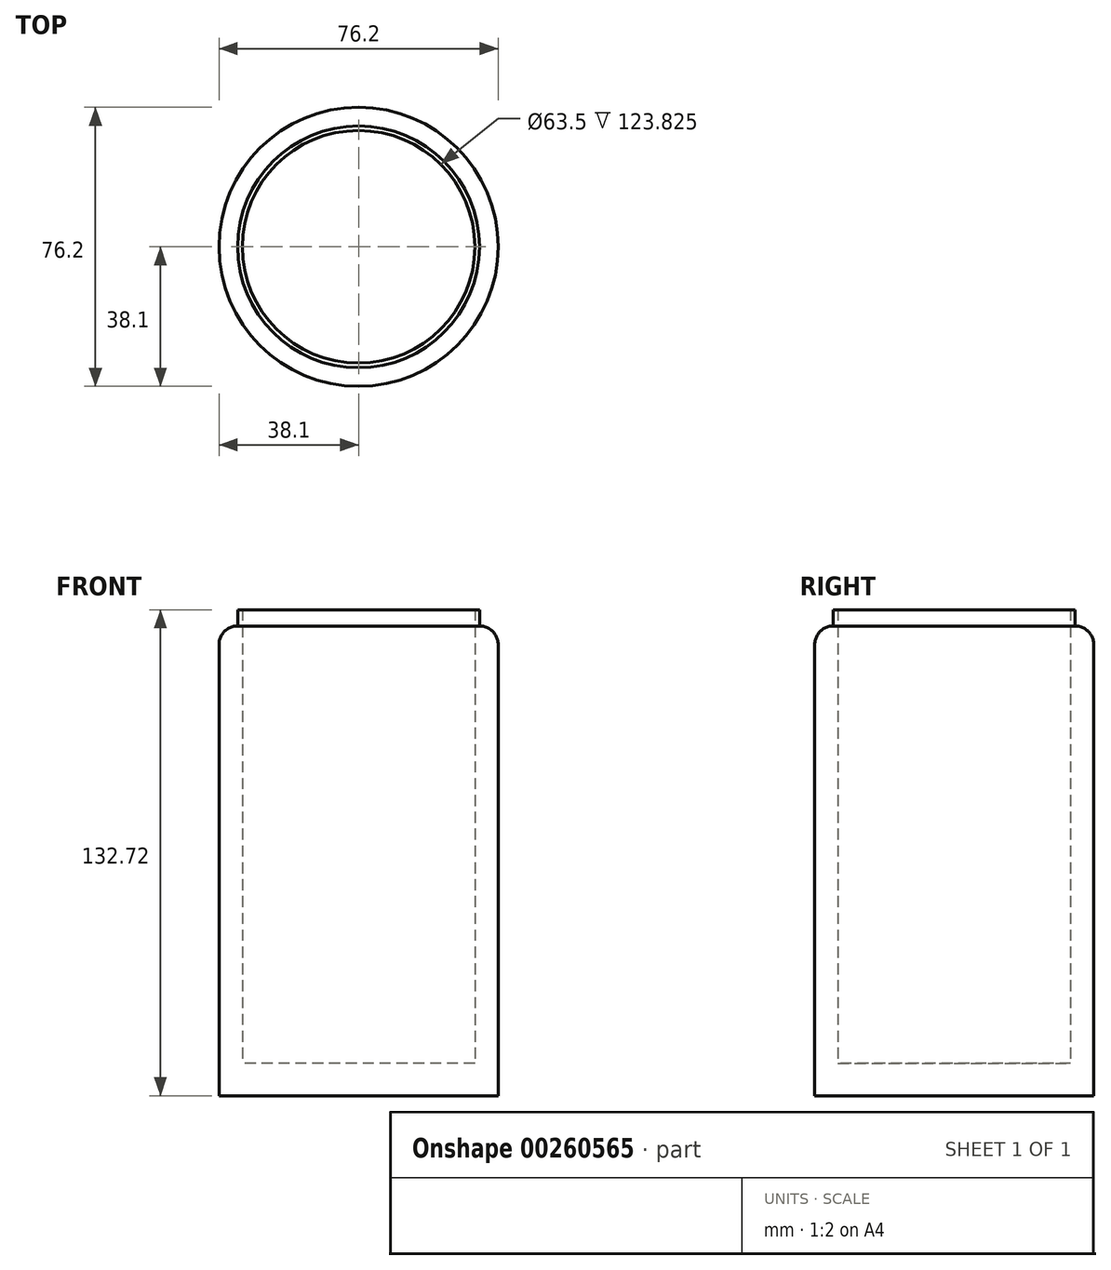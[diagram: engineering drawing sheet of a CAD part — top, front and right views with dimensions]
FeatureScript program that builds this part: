
annotation { "Feature Type Name" : "Feature", "Feature Type Description" : "" }
export const myFeature = defineFeature(function(context is Context, id is Id, definition is map)
    precondition{}
    {
        {
            var Q0;
            Q0=qCreatedBy(makeId("Top.planeOp"),FACE);
            var sketch = newSketch(context, id + "F0", { "sketchPlane" : qUnion([Q0])});
            skCircle(sketch, "E0", {"center": v(0, 0) * mm, "radius": 38.1 * mm});
            skCircle(sketch, "E1", {"center": v(0, 0) * mm, "radius": 31.75 * mm});
            skSolve(sketch);
        }
        {
            var Q0;
            Q0 = qSketchRegion(id + "F0", true);
            extrude(context, id + "F1", {"entities" : qUnion([Q0]), "depth" : 123.82 * mm});
        }
        {
            var Q0;
            Q0=makeQuery(id+"F1.opExtrude","CAP_EDGE",EDGE,{"disambiguationData":[OSD([sQuery(id+"F0.wireOp",EDGE,"E0")])],"isStart":false});
            fillet(context, id + "F2", {"entities" : qUnion([Q0]), "radius" : 5.08 * mm, "tangentPropagation" : true, "allowEdgeOverflow" : false});
        }
        {
            var Q0;
            Q0=makeQuery(id+"F0.imprint","IMPRINT",FACE,{"disambiguationData":[TD([[makeQuery(id+"F0.imprint","IMPRINT",EDGE,{"derivedFrom":sQuery(id+"F0.wireOp",EDGE,"E1")}),1.0]])]});
            var sketch = newSketch(context, id + "F3", { "sketchPlane" : qUnion([Q0])});
            skCircle(sketch, "E2", {"center": v(0, 0) * mm, "radius": 38.1 * mm});
            skSolve(sketch);
        }
        {
            var Q0;
            Q0=makeQuery(id+"F3.imprint","IMPRINT",FACE,{"disambiguationData":[TD([[makeQuery(id+"F3.imprint","IMPRINT",EDGE,{"derivedFrom":sQuery(id+"F3.wireOp",EDGE,"E2")}),1.0]])]});
            var Q1;
            Q1=makeQuery(id+"F3.imprint","IMPRINT",FACE,{"disambiguationData":[TD([[makeQuery(id+"F3.imprint","IMPRINT",EDGE,{"derivedFrom":makeQuery(id+"F0.imprint","IMPRINT",EDGE,{"derivedFrom":sQuery(id+"F0.wireOp",EDGE,"E1")})}),1.0]])]});
            var Q2;
            Q2=makeQuery(id+"F1.opExtrude","CAP_FACE",FACE,{"disambiguationData":[OSD([sQuery(id+"F0.wireOp",EDGE,"E0"),sQuery(id+"F0.wireOp",EDGE,"E1")])],"isStart":true});
            var Q3;
            Q3=makeQuery(id+"F0.imprint","IMPRINT",FACE,{"disambiguationData":[TD([[makeQuery(id+"F0.imprint","IMPRINT",EDGE,{"derivedFrom":sQuery(id+"F0.wireOp",EDGE,"E0")}),1.0]])]});
            var Q4;
            Q4=makeQuery(id+"F1.opExtrude","CAP_FACE",FACE,{"disambiguationData":[OSD([sQuery(id+"F0.wireOp",EDGE,"E0"),sQuery(id+"F0.wireOp",EDGE,"E1")])],"isStart":false});
            extrude(context, id + "F4", {"entities" : qUnion([Q0, Q1, Q2, Q3, Q4]), "operationType" : NewBodyOperationType.ADD, "endBound" : BoundingType.SYMMETRIC, "depth" : 8.9 * mm});
        }
    });
